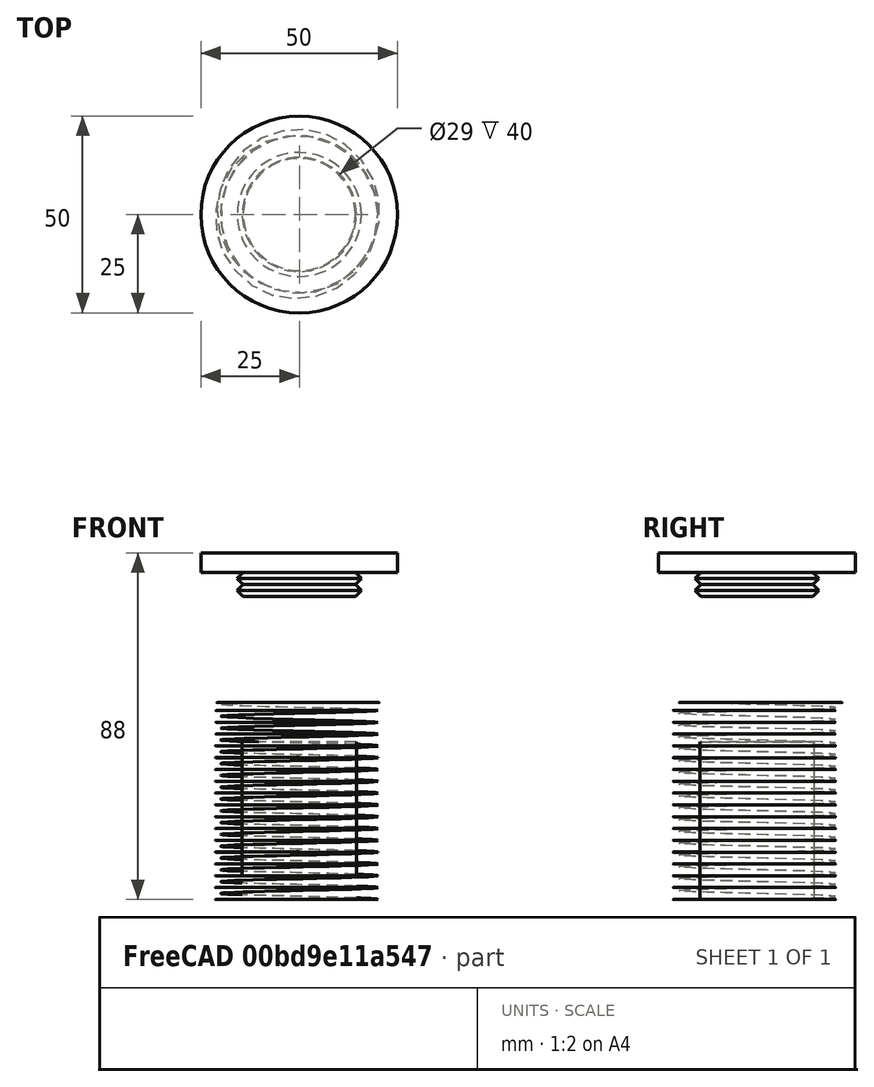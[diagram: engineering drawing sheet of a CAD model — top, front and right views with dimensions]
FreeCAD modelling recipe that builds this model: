
FCSTD DOCUMENT  (FreeCAD 2021.911R24301 +3846 (Git))
Label: leg extension
License: All rights reserved
LicenseURL: http://en.wikipedia.org/wiki/All_rights_reserved
objects: Sketcher::SketchObject×4, PartDesign::Body×3, Part::Part2DObjectPython×2, PartDesign::Pocket×2, PartDesign::AdditiveHelix×1, PartDesign::Pad×1, PartDesign::SubtractiveHelix×1, PartDesign::Revolution×1
note: 27 computed .brp shape members not serialized (recipe doc carries the construction recipe); baked Part::Feature solids carry a one-line shape summary decoded from their .brp

FEATURE [Part::Part2DObjectPython] VThreadProfile  # Draft 2D object (typed FeaturePython)
  Area = 1343.86
  Closed = true
  Continuity = C3
  Instructions = Expand this with the ... button to view instructions | Sweep this object along a helix of the same pitch to produce your thread. | It is recommended to make the helix in the ThreadProfile workbench. | If there is an active Body the ThreadProfile object will be put into it.,If not it can be dragged and dropped into the body later. | If there is an active Body when the helix is made there will be made a ShapeBinder for it | For internal threads you will need to cut the Sweep object out of a cylinder, or if using Part Design sweep it as a Subtractive Pipe. | Always use Frenet mode | I have provided some presets, but it is possible there could be some errors.  Double check for mission critical applications. | Also, the tolerances might be different from what you wish to have.  I believe the internal minor diameters are all minimum and the external are all maximum.
  InternalOrExternal = 1
  MakeFace = true
  MinorDiameter = 40
  Parameterization = 1
  Pitch = 3
  Points = (719) [(19.9922,0.174712,0),(19.9831,0.349292,0),(19.9728,0.523734,0),(19.9612,0.698031,0),(19.9483,0.872175,0),(19.9341,1.04616,0),(19.9186,1.21997,0),+712 more]
  Presets = 0
  Quality = 1
  ThreadCount = 20
  Version = 1.69
  external_data = [-0.00235387,-0.00461052,-0.00677828,-0.00886428,-0.0108747,-0.0128149,-0.0146895,-0.0165028,-0.0182584,-0.0199597,-0.0216095,-0.0232106,-0.0247653,-0.0262759,-0.0277444,-0.0291725,-0.0305621,-0.0319145,-0.0332313,-0.0345138,-0.0357632,+698 more]
  internal_data = [0,0,0,0,0,0,0,0,0,0,0,0,0,0,0,0,0,0,0,0,0,0,0,0,0,0,0,0,0,0,0,0,0,0,0,0,0,0,0,0,0,0,0,0,0,0,0,0,0,0,0,0,0,0,0,0,0,0,0,0,0,0,0,0,0,0,0,0,0,0,0,0,0,0,0,0,0,0,0,0,0,0,0,0,0,0,0,0,0,0,0,0,0,0,0,0,0,0,0,0,0,0,0,0,0,0,0,0,0,0,0,0,0,0,0,0,0,0,0,0,+599 more]
  preset_names = <blob: 3959 chars omitted>
  presets_data = [0,0,0,2.20878,24.1173,24.6888,0.25,0.693,0.729,0.25,0.793,0.829,0.25,0.893,0.929,0.3,1.032,1.075,0.35,1.171,1.221,0.35,1.371,1.421,0.4,1.509,1.567,0.45,1.648,1.713,0.45,1.948,2.013,0.5,2.387,2.459,0.6,2.764,2.85,0.7,3.141,3.242,0.75,3.58,+712 more]
FEATURE [PartDesign::AdditiveHelix] AdditiveHelix
  Angle = 0
  Axis = (-3e-16,3e-16,1)
  Base = (0,0,0)
  ClaimChildren = false
  Fit = 0
  FitJoin = 0
  HasBeenEdited = true
  Height = 50
  InnerFit = 0
  InnerFitJoin = 0
  LeftHanded = false
  Mode = 0
  NewSolid = false
  Outside = false
  Pitch = 3
  Profile = -> VThreadProfile
  ReferenceAxis = -> Z_Axis
  Refine = true
  Suppress = false
  Turns = 3
  _ProfileBasedVersion = 1
FEATURE [Sketcher::SketchObject] Sketch
  FullyConstrained = true
  MapMode = 5
  Placement = pos=(0,0,0) rot=(1,0,0;3.14159rad)
  Support = -> [AdditiveHelix]
  sketch-geometry (1):
    g0: Circle CenterX=0 CenterY=0 CenterZ=0 NormalX=0 NormalY=0 NormalZ=1 AngleXU=0 Radius=14.5
  constraints (2):
    c: Coincident(g0,g-1)
    c: Diameter(g0) = 29
FEATURE [PartDesign::Pocket] Pocket
  BaseFeature = -> AdditiveHelix
  ClaimChildren = false
  Fit = 0
  FitJoin = 0
  InnerFit = 0
  InnerFitJoin = 0
  InnerTaperAngle = 0
  InnerTaperAngleRev = 0
  Length = 40
  Length2 = 100
  Linearize = true
  NewSolid = false
  Profile = -> Sketch
  Refine = true
  Suppress = false
  Type = 0
  _ProfileBasedVersion = 1
FEATURE [PartDesign::Body] Body  label="leg cap"
  AutoGroupSolids = false
  ExportMode = 0
  Group = -> [VThreadProfile,AdditiveHelix,Sketch,Pocket]
  Origin = -> Origin
  Tip = -> Pocket
  _ExportChildren = -> [AdditiveHelix,Pocket]
  _GroupVersion = 1
FEATURE [Part::Part2DObjectPython] VThreadProfile001  # Draft 2D object (typed FeaturePython)
  Area = 1349.3
  Closed = true
  Continuity = C3
  Instructions = Expand this with the ... button to view instructions | Sweep this object along a helix of the same pitch to produce your thread. | It is recommended to make the helix in the ThreadProfile workbench. | If there is an active Body the ThreadProfile object will be put into it.,If not it can be dragged and dropped into the body later. | If there is an active Body when the helix is made there will be made a ShapeBinder for it | For internal threads you will need to cut the Sweep object out of a cylinder, or if using Part Design sweep it as a Subtractive Pipe. | Always use Frenet mode | I have provided some presets, but it is possible there could be some errors.  Double check for mission critical applications. | Also, the tolerances might be different from what you wish to have.  I believe the internal minor diameters are all minimum and the external are all maximum.
  InternalOrExternal = 0
  MakeFace = true
  MinorDiameter = 40
  Parameterization = 1
  Pitch = 3
  Placement = pos=(0,0,-0.1) rot=(0,0,1;0.785398rad)
  Points = (719) [(19.9992,0.174773,0),(19.9969,0.349534,0),(19.9931,0.524267,0),(19.9878,0.69896,0),(19.9809,0.8736,0),(19.9725,1.04817,0),(19.9626,1.22267,0),+712 more]
  Presets = 0
  Quality = 1
  ThreadCount = 20
  Version = 1.69
  external_data = [-0.00235387,-0.00461052,-0.00677828,-0.00886428,-0.0108747,-0.0128149,-0.0146895,-0.0165028,-0.0182584,-0.0199597,-0.0216095,-0.0232106,-0.0247653,-0.0262759,-0.0277444,-0.0291725,-0.0305621,-0.0319145,-0.0332313,-0.0345138,-0.0357632,+698 more]
  internal_data = [0,0,0,0,0,0,0,0,0,0,0,0,0,0,0,0,0,0,0,0,0,0,0,0,0,0,0,0,0,0,0,0,0,0,0,0,0,0,0,0,0,0,0,0,0,0,0,0,0,0,0,0,0,0,0,0,0,0,0,0,0,0,0,0,0,0,0,0,0,0,0,0,0,0,0,0,0,0,0,0,0,0,0,0,0,0,0,0,0,0,0,0,0,0,0,0,0,0,0,0,0,0,0,0,0,0,0,0,0,0,0,0,0,0,0,0,0,0,0,0,+599 more]
  preset_names = <blob: 3959 chars omitted>
  presets_data = [0,0,0,2.20878,24.1173,24.6888,0.25,0.693,0.729,0.25,0.793,0.829,0.25,0.893,0.929,0.3,1.032,1.075,0.35,1.171,1.221,0.35,1.371,1.421,0.4,1.509,1.567,0.45,1.648,1.713,0.45,1.948,2.013,0.5,2.387,2.459,0.6,2.764,2.85,0.7,3.141,3.242,0.75,3.58,+712 more]
FEATURE [Sketcher::SketchObject] Sketch001
  FullyConstrained = true
  MapMode = 5
  Support = -> [XY_Plane001]
  sketch-geometry (1):
    g0: Circle CenterX=0 CenterY=0 CenterZ=0 NormalX=0 NormalY=0 NormalZ=1 AngleXU=0 Radius=25
  constraints (2):
    c: Coincident(g0,g-1)
    c: Diameter(g0) = 50
FEATURE [PartDesign::Pad] Pad
  ClaimChildren = false
  Direction = (1,1,1)
  Fit = 0
  FitJoin = 0
  InnerFit = 0
  InnerFitJoin = 0
  InnerTaperAngle = 0
  InnerTaperAngleRev = 0
  Length = 65
  Length2 = 100
  Linearize = true
  NewSolid = false
  Profile = -> Sketch001
  Refine = true
  Suppress = false
  Type = 0
  _ProfileBasedVersion = 1
FEATURE [PartDesign::SubtractiveHelix] SubtractiveHelix
  Angle = 0
  Axis = (-3e-16,3e-16,1)
  Base = (0,0,0)
  BaseFeature = -> Pad
  ClaimChildren = false
  Fit = 0.5
  FitJoin = 0
  HasBeenEdited = true
  Height = 50
  InnerFit = 0
  InnerFitJoin = 0
  LeftHanded = false
  Mode = 0
  NewSolid = false
  Outside = true
  Pitch = 3
  Profile = -> VThreadProfile001
  ReferenceAxis = -> Z_Axis001
  Refine = true
  Suppress = false
  Turns = 3
  _ProfileBasedVersion = 1
FEATURE [Sketcher::SketchObject] Sketch002
  FullyConstrained = true
  MapMode = 5
  Placement = pos=(0,0,65) rot=(0,0,1;0rad)
  Support = -> [SubtractiveHelix]
  sketch-geometry (1):
    g0: Circle CenterX=0 CenterY=0 CenterZ=0 NormalX=0 NormalY=0 NormalZ=1 AngleXU=0 Radius=15
  constraints (2):
    c: Coincident(g0,g-1)
    c: Diameter(g0) = 30
FEATURE [PartDesign::Pocket] Pocket001
  BaseFeature = -> SubtractiveHelix
  ClaimChildren = false
  Fit = 0
  FitJoin = 0
  InnerFit = 0
  InnerFitJoin = 0
  InnerTaperAngle = 0
  InnerTaperAngleRev = 0
  Length = 8
  Length2 = 100
  Linearize = true
  NewSolid = false
  Profile = -> Sketch002
  Refine = true
  Suppress = false
  Type = 0
  _ProfileBasedVersion = 1
FEATURE [PartDesign::Body] Body001  label="extension"
  AutoGroupSolids = false
  ExportMode = 0
  Group = -> [VThreadProfile001,Sketch001,Pad,SubtractiveHelix,Sketch002,Pocket001]
  Origin = -> Origin001
  Placement = pos=(0,-1.78814e-06,15) rot=(0,0,1;0rad)
  Tip = -> Pocket001
  _ExportChildren = -> [Pad,SubtractiveHelix,Pocket001]
  _GroupVersion = 1
FEATURE [Sketcher::SketchObject] Sketch003
  AttachmentOffset = pos=(0,77,0) rot=(0,0,1;0rad)
  FullyConstrained = true
  MapMode = 5
  Placement = pos=(0,-1.71e-14,77) rot=(1,0,0;1.5708rad)
  Support = -> [XZ_Plane002]
  expr: Constraints[13] = 30 / 2
  sketch-geometry (10):
    g0: LineSegment StartX=14.25 StartY=0 StartZ=0 EndX=15.75 EndY=1.5 EndZ=0
    g1: LineSegment StartX=15.75 StartY=1.5 StartZ=0 EndX=14.25 EndY=3 EndZ=0
    g2: LineSegment StartX=14.25 StartY=3 StartZ=0 EndX=15.75 EndY=4.5 EndZ=0
    g3: LineSegment StartX=15.75 StartY=4.5 StartZ=0 EndX=14.25 EndY=6 EndZ=0
    g4: GeomPoint [constr] X=15 Y=0.75 Z=0
    g5: LineSegment StartX=14.25 StartY=6 StartZ=0 EndX=25 EndY=6 EndZ=0
    g6: LineSegment StartX=25 StartY=6 StartZ=0 EndX=25 EndY=11 EndZ=0
    g7: LineSegment StartX=14.25 StartY=0 StartZ=0 EndX=0 EndY=0 EndZ=0
    g8: LineSegment StartX=25 StartY=11 StartZ=0 EndX=0 EndY=11 EndZ=0
    g9: LineSegment StartX=0 StartY=11 StartZ=0 EndX=0 EndY=0 EndZ=0
  constraints (27):
    c: PointOnObject(g0,g-1)
    c: Coincident(g1,g0)
    c: Coincident(g2,g1)
    c: Coincident(g3,g2)
    c: Angle(g0) = 0.785398
    c: Angle(g1) = 2.35619
    c: Parallel(g0,g2)
    c: Equal(g0,g1)
    c: Equal(g1,g2)
    c: Equal(g2,g3)
    c: Parallel(g1,g3)
    c: DistanceY(g0,g3) = 6
    c: Symmetric(g0,g0,g4)
    c: DistanceX(g4) = 15
    c: Coincident(g5,g3)
    c: Horizontal(g5)
    c: DistanceX(g5) = 25
    c: Coincident(g6,g5)
    c: Vertical(g6)
    c: DistanceY(g6,g6) = 5
    c: Coincident(g7,g0)
    c: Coincident(g7,g-1)
    c: Coincident(g8,g6)
    c: Horizontal(g8)
    c: Vertical(g8,g7)
    c: Coincident(g9,g8)
    c: Coincident(g9,g7)
FEATURE [PartDesign::Revolution] Revolution
  Angle = 360
  Axis = (0,2e-16,1)
  Base = (0,1.71e-14,77)
  ClaimChildren = false
  Fit = 0
  FitJoin = 0
  InnerFit = 0
  InnerFitJoin = 0
  NewSolid = false
  Placement = pos=(0,0,0) rot=(1,0,0;1.5708rad)
  Profile = -> Sketch003
  ReferenceAxis = -> Sketch003 [V_Axis]
  Refine = true
  Reversed = true
  Suppress = false
  _ProfileBasedVersion = 1
FEATURE [PartDesign::Body] Body002  label="foot"
  AutoGroupSolids = false
  ExportMode = 0
  Group = -> [Sketch003,Revolution]
  Origin = -> Origin002
  Tip = -> Revolution
  _ExportChildren = -> [Revolution]
  _GroupVersion = 1
